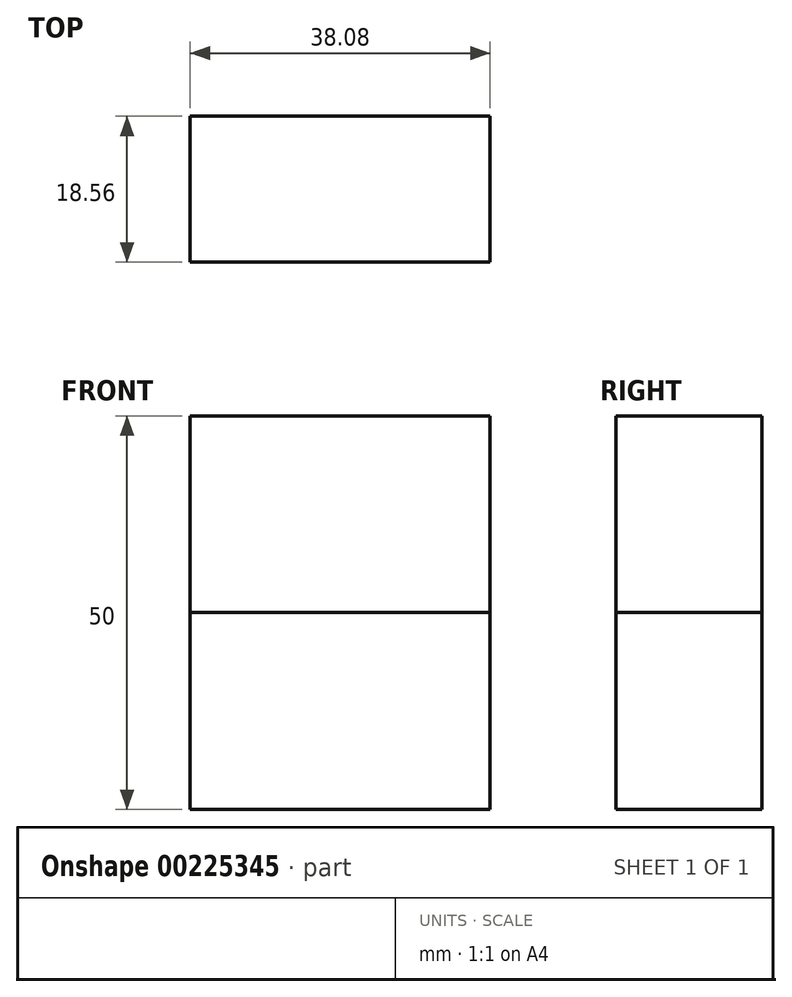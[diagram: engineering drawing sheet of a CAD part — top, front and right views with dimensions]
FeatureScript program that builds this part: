
annotation { "Feature Type Name" : "Feature", "Feature Type Description" : "" }
export const myFeature = defineFeature(function(context is Context, id is Id, definition is map)
    precondition{}
    {
        {
            var Q0;
            Q0=qCreatedBy(makeId("Top.planeOp"),FACE);
            var sketch = newSketch(context, id + "F0", { "sketchPlane" : qUnion([Q0])});
            skLineSegment(sketch, "E0.bottom", {"start": v(8.02, -9.28) * mm, "end": v(-92.3, -9.28) * mm});
            skLineSegment(sketch, "E0.top", {"start": v(8.02, 48.73) * mm, "end": v(-92.3, 48.73) * mm});
            skLineSegment(sketch, "E0.left", {"start": v(8.02, -9.28) * mm, "end": v(8.02, 48.73) * mm});
            skLineSegment(sketch, "E0.right", {"start": v(-92.3, -9.28) * mm, "end": v(-92.3, 48.73) * mm});
            skPoint(sketch, "E0.middle", {"position": v(-42.14, 19.73) * mm});
            skLineSegment(sketch, "E1.bottom", {"start": v(-30.06, 9.28) * mm, "end": v(8.02, 9.28) * mm});
            skLineSegment(sketch, "E1.top", {"start": v(-30.06, -9.28) * mm, "end": v(8.02, -9.28) * mm});
            skLineSegment(sketch, "E1.left", {"start": v(-30.06, 9.28) * mm, "end": v(-30.06, -9.28) * mm});
            skLineSegment(sketch, "E1.right", {"start": v(8.02, 9.28) * mm, "end": v(8.02, -9.28) * mm});
            skPoint(sketch, "E1.middle", {"position": v(-11.02, 0) * mm});
            skLineSegment(sketch, "E2", {"start": v(-113.32, 56.93) * mm, "end": v(-113.32, -24.38) * mm, "construction": true});
            skLineSegment(sketch, "E3", {"start": v(-133.73, 28.04) * mm, "end": v(-133.73, 9.52) * mm});
            skLineSegment(sketch, "E4", {"start": v(-133.73, 9.52) * mm, "end": v(-156.18, 9.52) * mm});
            skLineSegment(sketch, "E5", {"start": v(-156.18, 9.52) * mm, "end": v(-156.18, 21.92) * mm});
            skLineSegment(sketch, "E6", {"start": v(-156.18, 21.92) * mm, "end": v(-144.4, 15.64) * mm});
            skLineSegment(sketch, "E7", {"start": v(-144.4, 15.64) * mm, "end": v(-144.4, 32.91) * mm});
            skLineSegment(sketch, "E8", {"start": v(-144.4, 32.91) * mm, "end": v(-133.73, 28.04) * mm});
            skLineSegment(sketch, "E9.bottom", {"start": v(-139.07, -18.58) * mm, "end": v(-167.17, -18.58) * mm});
            skLineSegment(sketch, "E9.top", {"start": v(-139.07, -0.37) * mm, "end": v(-167.17, -0.37) * mm});
            skLineSegment(sketch, "E9.left", {"start": v(-139.07, -18.58) * mm, "end": v(-139.07, -0.37) * mm});
            skLineSegment(sketch, "E9.right", {"start": v(-167.17, -18.58) * mm, "end": v(-167.17, -0.37) * mm});
            skPoint(sketch, "E9.middle", {"position": v(-153.12, -9.47) * mm});
            skSolve(sketch);
        }
        {
            var Q0;
            Q0=makeQuery(id+"F0.imprint","IMPRINT",FACE,{"disambiguationData":[TD([[makeQuery(id+"F0.imprint","IMPRINT",EDGE,{"derivedFrom":sQuery(id+"F0.wireOp",EDGE,"E0.bottom")}),-1.0]])]});
            extrude(context, id + "F1", {"entities" : qUnion([Q0]), "depth" : 25 * mm});
        }
        {
            var Q0;
            Q0=makeQuery(id+"F0.imprint","IMPRINT",FACE,{"disambiguationData":[TD([[makeQuery(id+"F0.imprint","IMPRINT",EDGE,{"derivedFrom":sQuery(id+"F0.wireOp",EDGE,"E1.bottom")}),-1.0]])]});
            extrude(context, id + "F2", {"entities" : qUnion([Q0]), "depth" : 25 * mm});
        }
        {
            var Q0;
            Q0=makeQuery(id+"F2.opExtrude","CAP_FACE",FACE,{"disambiguationData":[OSD([sQuery(id+"F0.wireOp",EDGE,"E1.bottom"),sQuery(id+"F0.wireOp",EDGE,"E1.top"),sQuery(id+"F0.wireOp",EDGE,"E1.left"),sQuery(id+"F0.wireOp",EDGE,"E1.right")])],"isStart":false});
            extrude(context, id + "F3", {"entities" : qUnion([Q0]), "depth" : 25 * mm});
        }
    });
